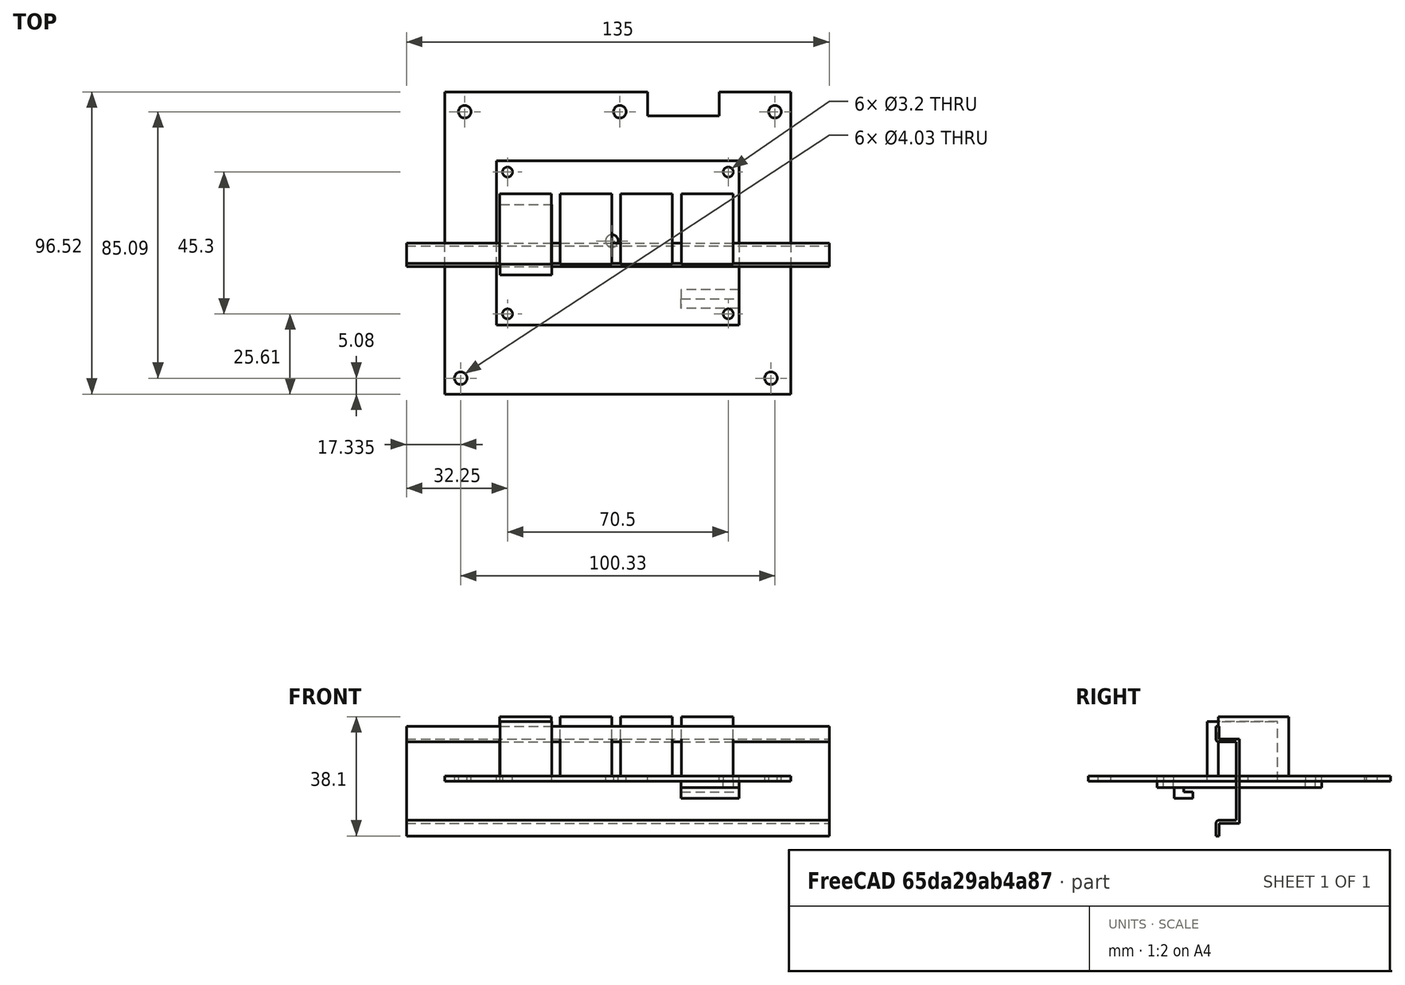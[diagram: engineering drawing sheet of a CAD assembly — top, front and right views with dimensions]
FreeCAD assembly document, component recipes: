
FREECAD ASSEMBLY — COMPONENT RECIPES ("autopool_box19")

This assembly document has 4 components, labeled P0..P3 below (a component is one placed body or linked part). 4 of them carry a construction recipe — the FreeCAD feature program that regenerates the part from scratch, quoted from this document or its linked companion documents; the rest are supplied as boundary geometry only. No exploded tour is included for this assembly.
COMPONENT P0 — recipe-attached ("support001", modeled in this document).
Construction recipe (the document's own serialized feature program — sketch geometry with constraints, then the solid features built on it; lengths are millimeters unless a unit is written):

FEATURE [PartDesign::ShapeBinder] ShapeBinder
  Support = -> [LinearPattern]
  TraceSupport = false
FEATURE [Sketcher::SketchObject] Sketch006
  ExternalGeometry = -> [ShapeBinder]
  MapMode = 5
  Placement = pos=(0,0,0) rot=(1,0,0;3.14159rad)
  Support = -> [ShapeBinder]
  sketch-geometry (6):
    g0: LineSegment StartX=38.75 StartY=26.25 StartZ=0 EndX=20.2255 EndY=26.25 EndZ=0
    g1: LineSegment StartX=20.2255 StartY=26.25 StartZ=0 EndX=20.2255 EndY=-26.25 EndZ=0
    g2: LineSegment StartX=20.2255 StartY=-26.25 StartZ=0 EndX=38.75 EndY=-26.25 EndZ=0
    g3: LineSegment StartX=38.75 StartY=-26.25 StartZ=0 EndX=38.75 EndY=26.25 EndZ=0
    g4: Circle CenterX=35.25 CenterY=-22.65 CenterZ=0 NormalX=0 NormalY=0 NormalZ=1 AngleXU=0 Radius=1.6
    g5: Circle CenterX=35.25 CenterY=22.65 CenterZ=0 NormalX=0 NormalY=0 NormalZ=1 AngleXU=0 Radius=1.6
  constraints (12):
    c: Coincident(g0,g1)
    c: Coincident(g1,g2)
    c: Coincident(g2,g3)
    c: Coincident(g3,g0)
    c: Horizontal(g0)
    c: Horizontal(g2)
    c: Vertical(g1)
    c: Vertical(g3)
    c: Coincident(g0,g-4)
    c: PointOnObject(g1,g-5)
    c: Coincident(g4,g-6)
    c: Coincident(g5,g-7)
FEATURE [PartDesign::Pad] Pad006
  AllowMultiFace = false
  Length = 2
  Length2 = 100
  Profile = -> Sketch006
  Type = 0
FEATURE [PartDesign::Body] Body005  label="base"
  Group = -> [ShapeBinder,Sketch006,Pad006]
  Origin = -> Origin009
  Tip = -> Pad006
FEATURE [PartDesign::ShapeBinder] ShapeBinder001
  Placement = pos=(0,0,-2) rot=(0,0,1;0rad)
  Support = -> [Pad006]
  TraceSupport = false
FEATURE [Sketcher::SketchObject] Sketch009
  ExternalGeometry = -> [ShapeBinder001]
  MapMode = 5
  Placement = pos=(0,0,-2) rot=(1,0,0;3.14159rad)
  Support = -> [ShapeBinder001]
  sketch-geometry (4):
    g0: LineSegment StartX=20.2255 StartY=-17.8362 StartZ=0 EndX=38.75 EndY=-17.8362 EndZ=0
    g1: LineSegment StartX=38.75 StartY=-17.8362 StartZ=0 EndX=38.75 EndY=-20.8846 EndZ=0
    g2: LineSegment StartX=38.75 StartY=-20.8846 StartZ=0 EndX=20.2255 EndY=-20.8846 EndZ=0
    g3: LineSegment StartX=20.2255 StartY=-20.8846 StartZ=0 EndX=20.2255 EndY=-17.8362 EndZ=0
  constraints (10):
    c: Coincident(g0,g1)
    c: Coincident(g1,g2)
    c: Coincident(g2,g3)
    c: Coincident(g3,g0)
    c: Horizontal(g0)
    c: Horizontal(g2)
    c: Vertical(g1)
    c: Vertical(g3)
    c: PointOnObject(g0,g-3)
    c: PointOnObject(g1,g-4)
FEATURE [PartDesign::Pad] Pad009
  AllowMultiFace = false
  Length = 1.5
  Length2 = 100
  Placement = pos=(0,0,-2) rot=(0,0,1;0rad)
  Profile = -> Sketch009
  Type = 0
FEATURE [Sketcher::SketchObject] Sketch010
  ExternalGeometry = -> [Pad009]
  MapMode = 5
  Placement = pos=(0,0,-3.5) rot=(1,0,0;3.14159rad)
  Support = -> [Pad009]
  sketch-geometry (4):
    g0: LineSegment StartX=20.2255 StartY=-20.8846 StartZ=0 EndX=38.75 EndY=-20.8846 EndZ=0
    g1: LineSegment StartX=38.75 StartY=-20.8846 StartZ=0 EndX=38.75 EndY=-14.8508 EndZ=0
    g2: LineSegment StartX=38.75 StartY=-14.8508 StartZ=0 EndX=20.2255 EndY=-14.8508 EndZ=0
    g3: LineSegment StartX=20.2255 StartY=-14.8508 StartZ=0 EndX=20.2255 EndY=-20.8846 EndZ=0
  constraints (10):
    c: Coincident(g0,g1)
    c: Coincident(g1,g2)
    c: Coincident(g2,g3)
    c: Coincident(g3,g0)
    c: Horizontal(g0)
    c: Horizontal(g2)
    c: Vertical(g1)
    c: Vertical(g3)
    c: Coincident(g0,g-3)
    c: PointOnObject(g1,g-4)
FEATURE [PartDesign::Pad] Pad010
  AllowMultiFace = false
  BaseFeature = -> Pad009
  Length = 2
  Length2 = 100
  Placement = pos=(0,0,-2) rot=(0,0,1;0rad)
  Profile = -> Sketch010
  Type = 0
FEATURE [PartDesign::Body] Body006
  Group = -> [ShapeBinder001,Sketch009,Pad009,Sketch010,Pad010]
  Origin = -> Origin010
  Tip = -> Pad010
COMPONENT P1 — recipe-attached ("relays4_part", modeled in this document).
Construction recipe (the document's own serialized feature program — sketch geometry with constraints, then the solid features built on it; lengths are millimeters unless a unit is written):

FEATURE [Sketcher::SketchObject] Sketch
  MapMode = 5
  Support = -> [XY_Plane001]
  sketch-geometry (12):
    g0: LineSegment StartX=-38.75 StartY=26.25 StartZ=0 EndX=38.75 EndY=26.25 EndZ=0
    g1: LineSegment StartX=38.75 StartY=26.25 StartZ=0 EndX=38.75 EndY=-26.25 EndZ=0
    g2: LineSegment StartX=38.75 StartY=-26.25 StartZ=0 EndX=-38.75 EndY=-26.25 EndZ=0
    g3: LineSegment StartX=-38.75 StartY=-26.25 StartZ=0 EndX=-38.75 EndY=26.25 EndZ=0
    g4: Circle CenterX=-35.25 CenterY=22.65 CenterZ=0 NormalX=0 NormalY=0 NormalZ=1 AngleXU=0 Radius=1.6
    g5: Circle CenterX=-35.25 CenterY=-22.65 CenterZ=0 NormalX=0 NormalY=0 NormalZ=1 AngleXU=0 Radius=1.6
    g6: Circle CenterX=35.25 CenterY=22.65 CenterZ=0 NormalX=0 NormalY=0 NormalZ=1 AngleXU=0 Radius=1.6
    g7: Circle CenterX=35.25 CenterY=-22.65 CenterZ=0 NormalX=0 NormalY=0 NormalZ=1 AngleXU=0 Radius=1.6
    g8: LineSegment [constr] StartX=-35.25 StartY=22.65 StartZ=0 EndX=35.25 EndY=22.65 EndZ=0
    g9: LineSegment [constr] StartX=35.25 StartY=22.65 StartZ=0 EndX=35.25 EndY=-22.65 EndZ=0
    g10: LineSegment [constr] StartX=35.25 StartY=-22.65 StartZ=0 EndX=-35.25 EndY=-22.65 EndZ=0
    g11: LineSegment [constr] StartX=-35.25 StartY=-22.65 StartZ=0 EndX=-35.25 EndY=22.65 EndZ=0
  constraints (31):
    c: Coincident(g0,g1)
    c: Coincident(g1,g2)
    c: Coincident(g2,g3)
    c: Coincident(g3,g0)
    c: Horizontal(g0)
    c: Horizontal(g2)
    c: Vertical(g1)
    c: Vertical(g3)
    c: Symmetric(g0,g1,g-1)
    c: DistanceX(g0,g0) = 77.5
    c: DistanceY(g1,g0) = 52.5
    c: DistanceY(g4,g0) = 3.6
    c: DistanceX(g0,g4) = 3.5
    c: Diameter(g4) = 3.2
    c: Equal(g4,g5)
    c: Equal(g5,g7)
    c: Equal(g7,g6)
    c: Coincident(g8,g9)
    c: Coincident(g9,g10)
    c: Coincident(g10,g11)
    c: Coincident(g11,g8)
    c: Horizontal(g8)
    c: Horizontal(g10)
    c: Vertical(g9)
    c: Vertical(g11)
    c: Coincident(g8,g4)
    c: DistanceX(g9,g1) = 3.5
    c: DistanceY(g1,g9) = 3.6
    c: Coincident(g6,g8)
    c: Coincident(g5,g10)
    c: Coincident(g7,g9)
FEATURE [PartDesign::Pad] Pad
  AllowMultiFace = false
  Length = 1.6
  Length2 = 100
  Profile = -> Sketch
  Type = 0
FEATURE [Sketcher::SketchObject] Sketch003
  MapMode = 5
  Support = -> [XY_Plane006]
  sketch-geometry (4):
    g0: LineSegment StartX=-37.6149 StartY=12.2539 StartZ=0 EndX=-21.1149 EndY=12.2539 EndZ=0
    g1: LineSegment StartX=-21.1149 StartY=12.2539 StartZ=0 EndX=-21.1149 EndY=-10.2461 EndZ=0
    g2: LineSegment StartX=-21.1149 StartY=-10.2461 StartZ=0 EndX=-37.6149 EndY=-10.2461 EndZ=0
    g3: LineSegment StartX=-37.6149 StartY=-10.2461 StartZ=0 EndX=-37.6149 EndY=12.2539 EndZ=0
  constraints (10):
    c: Coincident(g0,g1)
    c: Coincident(g1,g2)
    c: Coincident(g2,g3)
    c: Coincident(g3,g0)
    c: Horizontal(g0)
    c: Horizontal(g2)
    c: Vertical(g1)
    c: Vertical(g3)
    c: DistanceY(g1,g1) = 22.5
    c: DistanceX(g2,g2) = 16.5
FEATURE [PartDesign::Pad] Pad003
  AllowMultiFace = false
  Length = 19
  Length2 = 100
  Profile = -> Sketch003
  Type = 0
FEATURE [PartDesign::Body] Body003
  Group = -> [Sketch003,Pad003]
  Origin = -> Origin006
  Tip = -> Pad003
FEATURE [Sketcher::SketchObject] Sketch004
  MapMode = 5
  Placement = pos=(0,0,1.6) rot=(0,0,1;0rad)
  Support = -> [Pad]
  sketch-geometry (4):
    g0: LineSegment StartX=-37.75 StartY=15.7124 StartZ=0 EndX=-21.25 EndY=15.7124 EndZ=0
    g1: LineSegment StartX=-21.25 StartY=15.7124 StartZ=0 EndX=-21.25 EndY=-6.78761 EndZ=0
    g2: LineSegment StartX=-21.25 StartY=-6.78761 StartZ=0 EndX=-37.75 EndY=-6.78761 EndZ=0
    g3: LineSegment StartX=-37.75 StartY=-6.78761 StartZ=0 EndX=-37.75 EndY=15.7124 EndZ=0
  constraints (10):
    c: Coincident(g0,g1)
    c: Coincident(g1,g2)
    c: Coincident(g2,g3)
    c: Coincident(g3,g0)
    c: Horizontal(g0)
    c: Horizontal(g2)
    c: Vertical(g1)
    c: Vertical(g3)
    c: DistanceY(g1,g1) = 22.5
    c: DistanceX(g0,g0) = 16.5
FEATURE [PartDesign::Pad] Pad004
  AllowMultiFace = false
  BaseFeature = -> Pad
  Length = 19
  Length2 = 100
  Profile = -> Sketch004
  Type = 0
FEATURE [PartDesign::LinearPattern] LinearPattern
  BaseFeature = -> Pad004
  Direction = -> X_Axis001
  Length = 58
  Occurrences = 4
  Originals = -> [Pad004]
FEATURE [PartDesign::Body] Body
  Group = -> [Sketch,Pad,Sketch004,Pad004,LinearPattern]
  Origin = -> Origin001
  Tip = -> LinearPattern
COMPONENT P2 — recipe-attached ("autopool_part", modeled in this document).
Construction recipe (the document's own serialized feature program — sketch geometry with constraints, then the solid features built on it; lengths are millimeters unless a unit is written):

FEATURE [Sketcher::SketchObject] Sketch001
  MapMode = 5
  Support = -> [XY_Plane003]
  sketch-geometry (16):
    g0: LineSegment StartX=-55.245 StartY=48.26 StartZ=0 EndX=9.525 EndY=48.26 EndZ=0
    g1: LineSegment StartX=9.525 StartY=48.26 StartZ=0 EndX=9.525 EndY=40.64 EndZ=0
    g2: LineSegment StartX=9.525 StartY=40.64 StartZ=0 EndX=32.385 EndY=40.64 EndZ=0
    g3: LineSegment StartX=32.385 StartY=40.64 StartZ=0 EndX=32.385 EndY=48.26 EndZ=0
    g4: LineSegment StartX=32.385 StartY=48.26 StartZ=0 EndX=55.245 EndY=48.26 EndZ=0
    g5: LineSegment StartX=55.245 StartY=48.26 StartZ=0 EndX=55.245 EndY=-48.26 EndZ=0
    g6: LineSegment StartX=55.245 StartY=-48.26 StartZ=0 EndX=-55.245 EndY=-48.26 EndZ=0
    g7: LineSegment StartX=-55.245 StartY=-48.26 StartZ=0 EndX=-55.245 EndY=48.26 EndZ=0
    g8: LineSegment [constr] StartX=-48.895 StartY=41.91 StartZ=0 EndX=50.165 EndY=41.91 EndZ=0
    g9: LineSegment [constr] StartX=-50.165 StartY=-43.18 StartZ=0 EndX=48.895 EndY=-43.18 EndZ=0
    g10: Circle CenterX=-48.895 CenterY=41.91 CenterZ=0 NormalX=0 NormalY=0 NormalZ=1 AngleXU=0 Radius=2.015
    g11: Circle CenterX=-50.165 CenterY=-43.18 CenterZ=0 NormalX=0 NormalY=0 NormalZ=1 AngleXU=0 Radius=2.015
    g12: Circle CenterX=48.895 CenterY=-43.18 CenterZ=0 NormalX=0 NormalY=0 NormalZ=1 AngleXU=0 Radius=2.015
    g13: Circle CenterX=50.165 CenterY=41.91 CenterZ=0 NormalX=0 NormalY=0 NormalZ=1 AngleXU=0 Radius=2.015
    g14: Circle CenterX=0.635 CenterY=41.91 CenterZ=0 NormalX=0 NormalY=0 NormalZ=1 AngleXU=0 Radius=2.015
    g15: Circle CenterX=-1.905 CenterY=0.635 CenterZ=0 NormalX=0 NormalY=0 NormalZ=1 AngleXU=0 Radius=2.015
  constraints (45):
    c: Horizontal(g0)
    c: Coincident(g0,g1)
    c: Vertical(g1)
    c: Coincident(g1,g2)
    c: Horizontal(g2)
    c: Coincident(g2,g3)
    c: Vertical(g3)
    c: Coincident(g3,g4)
    c: Horizontal(g4)
    c: Coincident(g4,g5)
    c: Vertical(g5)
    c: Coincident(g5,g6)
    c: Horizontal(g6)
    c: Coincident(g6,g7)
    c: Coincident(g7,g0)
    c: Vertical(g7)
    c: Equal(g5,g7)
    c: DistanceY(g5,g4) = 96.52
    c: DistanceX(g3,g4) = 22.86
    c: DistanceX(g1,g2) = 22.86
    c: DistanceY(g1,g0) = 7.62
    c: DistanceX(g0,g0) = 64.77
    c: Symmetric(g0,g5,g-1)
    c: Horizontal(g8)
    c: DistanceY(g8,g0) = 6.35
    c: DistanceX(g8,g4) = 5.08
    c: DistanceX(g0,g8) = 6.35
    c: Horizontal(g9)
    c: DistanceX(g9,g5) = 6.35
    c: DistanceX(g6,g9) = 5.08
    c: DistanceY(g5,g9) = 5.08
    c: Coincident(g10,g8)
    c: Coincident(g11,g9)
    c: Coincident(g12,g9)
    c: Coincident(g13,g8)
    c: PointOnObject(g14,g8)
    c: Equal(g10,g14)
    c: Equal(g14,g13)
    c: Equal(g13,g12)
    c: Equal(g12,g11)
    c: Equal(g15,g13)
    c: Diameter(g15) = 4.03
    c: DistanceX(g14,g1) = 8.89
    c: DistanceX(g15,g5) = 57.15
    c: DistanceY(g5,g15) = 48.895
FEATURE [PartDesign::Pad] Pad001
  AllowMultiFace = false
  Length = 1.6
  Length2 = 100
  Profile = -> Sketch001
  Type = 0
FEATURE [PartDesign::Body] Body001
  Group = -> [Sketch001,Pad001]
  Origin = -> Origin003
  Tip = -> Pad001
COMPONENT P3 — recipe-attached ("din_rail_part", modeled in this document).
Construction recipe (the document's own serialized feature program — sketch geometry with constraints, then the solid features built on it; lengths are millimeters unless a unit is written):

FEATURE [Sketcher::SketchObject] Sketch005
  MapMode = 5
  Placement = pos=(0,0,0) rot=(0.57735,0.57735,0.57735;2.0944rad)
  Support = -> [YZ_Plane007]
  sketch-geometry (12):
    g0: LineSegment StartX=0 StartY=13.5 StartZ=0 EndX=0 EndY=-13.5 EndZ=0
    g1: LineSegment StartX=0 StartY=-13.5 StartZ=0 EndX=-6.5 EndY=-13.5 EndZ=0
    g2: LineSegment StartX=-6.5 StartY=-13.5 StartZ=0 EndX=-6.5 EndY=-17.5 EndZ=0
    g3: LineSegment StartX=-6.5 StartY=-17.5 StartZ=0 EndX=-7.5 EndY=-17.5 EndZ=0
    g4: LineSegment StartX=-7.5 StartY=-17.5 StartZ=0 EndX=-7.5 EndY=-12.5 EndZ=0
    g5: LineSegment StartX=-7.5 StartY=-12.5 StartZ=0 EndX=-1 EndY=-12.5 EndZ=0
    g6: LineSegment StartX=-1 StartY=-12.5 StartZ=0 EndX=-1 EndY=12.5 EndZ=0
    g7: LineSegment StartX=-1 StartY=12.5 StartZ=0 EndX=-7.5 EndY=12.5 EndZ=0
    g8: LineSegment StartX=-7.5 StartY=12.5 StartZ=0 EndX=-7.5 EndY=17.5 EndZ=0
    g9: LineSegment StartX=-7.5 StartY=17.5 StartZ=0 EndX=-6.5 EndY=17.5 EndZ=0
    g10: LineSegment StartX=-6.5 StartY=17.5 StartZ=0 EndX=-6.5 EndY=13.5 EndZ=0
    g11: LineSegment StartX=-6.5 StartY=13.5 StartZ=0 EndX=0 EndY=13.5 EndZ=0
  constraints (34):
    c: PointOnObject(g0,g-2)
    c: PointOnObject(g0,g-2)
    c: Coincident(g0,g1)
    c: Horizontal(g1)
    c: Coincident(g1,g2)
    c: Vertical(g2)
    c: Coincident(g2,g3)
    c: Coincident(g3,g4)
    c: Vertical(g4)
    c: Coincident(g4,g5)
    c: Horizontal(g5)
    c: Coincident(g5,g6)
    c: Coincident(g6,g7)
    c: Horizontal(g7)
    c: Coincident(g7,g8)
    c: Vertical(g8)
    c: Coincident(g8,g9)
    c: Coincident(g9,g10)
    c: Coincident(g10,g11)
    c: Coincident(g11,g0)
    c: Horizontal(g11)
    c: Horizontal(g9)
    c: Horizontal(g3)
    c: Equal(g9,g3)
    c: DistanceX(g6,g0) = 1
    c: DistanceX(g8,g9) = 1
    c: DistanceY(g7,g10) = 1
    c: DistanceY(g1,g4) = 1
    c: Symmetric(g6,g5,g-1)
    c: Equal(g11,g1)
    c: DistanceY(g3,g8) = 35
    c: DistanceX(g3,g0) = 7.5
    c: DistanceY(g0,g0) = 27
    c: Symmetric(g9,g2,g-1)
FEATURE [PartDesign::Pad] Pad005
  AllowMultiFace = false
  Length = 135
  Length2 = 100
  Midplane = true
  Placement = pos=(0,0,0) rot=(0.57735,0.57735,0.57735;2.0944rad)
  Profile = -> Sketch005
  Type = 0
FEATURE [PartDesign::Fillet] Fillet
  Base = -> Pad005 [Edge14]
  BaseFeature = -> Pad005
  Placement = pos=(0,0,0) rot=(0.57735,0.57735,0.57735;2.0944rad)
  Radius = 1
  SupportTransform = false
FEATURE [PartDesign::Fillet] Fillet001
  Base = -> Fillet [Edge35]
  BaseFeature = -> Fillet
  Placement = pos=(0,0,0) rot=(0.57735,0.57735,0.57735;2.0944rad)
  Radius = 1
  SupportTransform = false
FEATURE [PartDesign::Body] Body004
  Group = -> [Sketch005,Pad005,Fillet,Fillet001]
  Origin = -> Origin007
  Tip = -> Fillet001
PROVENANCE & LICENSES
A FreeCAD (.FCStd) document from a public repository crawl; recipes are the document's own serialized feature recipes (and, for linked parts, companion documents' recipes).
License: as declared in the source repository (recorded in the dataset sidecar).
